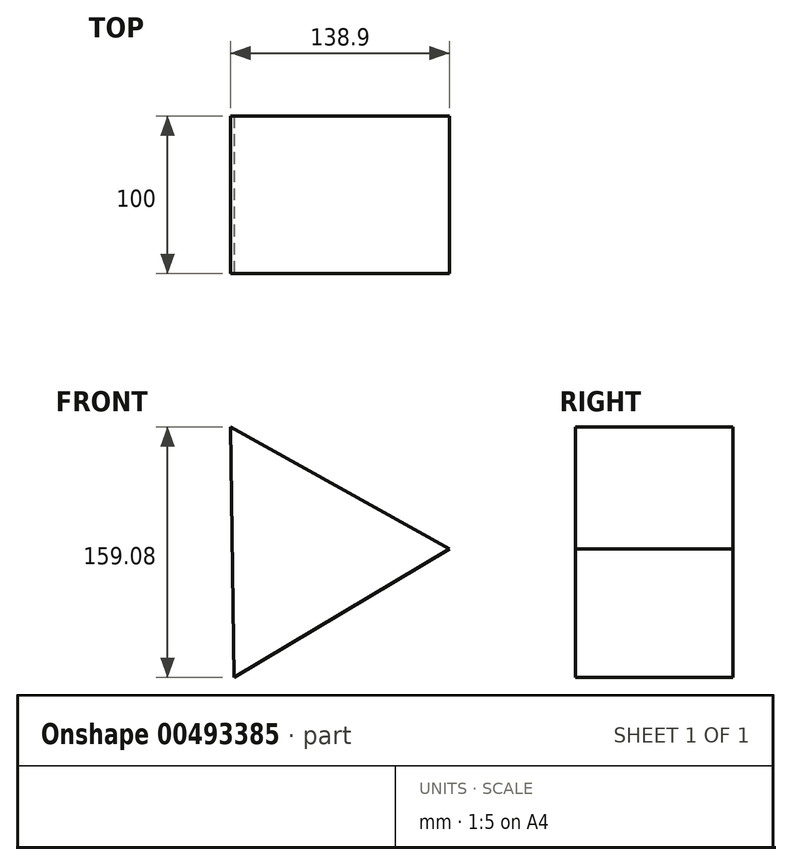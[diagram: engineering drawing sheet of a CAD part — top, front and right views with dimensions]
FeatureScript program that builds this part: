
annotation { "Feature Type Name" : "Feature", "Feature Type Description" : "" }
export const myFeature = defineFeature(function(context is Context, id is Id, definition is map)
    precondition{}
    {
        {
            var Q0;
            Q0=qCreatedBy(makeId("Front.planeOp"),FACE);
            var sketch = newSketch(context, id + "F0", { "sketchPlane" : qUnion([Q0])});
            skCircle(sketch, "E0.cCircle", {"center": v(0, 0) * mm, "radius": 45.93 * mm, "construction": true});
            skLineSegment(sketch, "E0.0", {"start": v(91.85, 1.3) * mm, "end": v(-44.8, -80.2) * mm});
            skLineSegment(sketch, "E0.1", {"start": v(-44.8, -80.2) * mm, "end": v(-47.05, 78.9) * mm});
            skLineSegment(sketch, "E0.2", {"start": v(-47.05, 78.9) * mm, "end": v(91.85, 1.3) * mm});
            skPoint(sketch, "E0.0.midPoint", {"position": v(23.52, -39.45) * mm});
            skSolve(sketch);
        }
        {
            var Q0;
            Q0 = qSketchRegion(id + "F0", true);
            extrude(context, id + "F1", {"entities" : qUnion([Q0]), "endBound" : BoundingType.SYMMETRIC, "oppositeDirection" : true, "depth" : 100 * mm});
        }
    });
